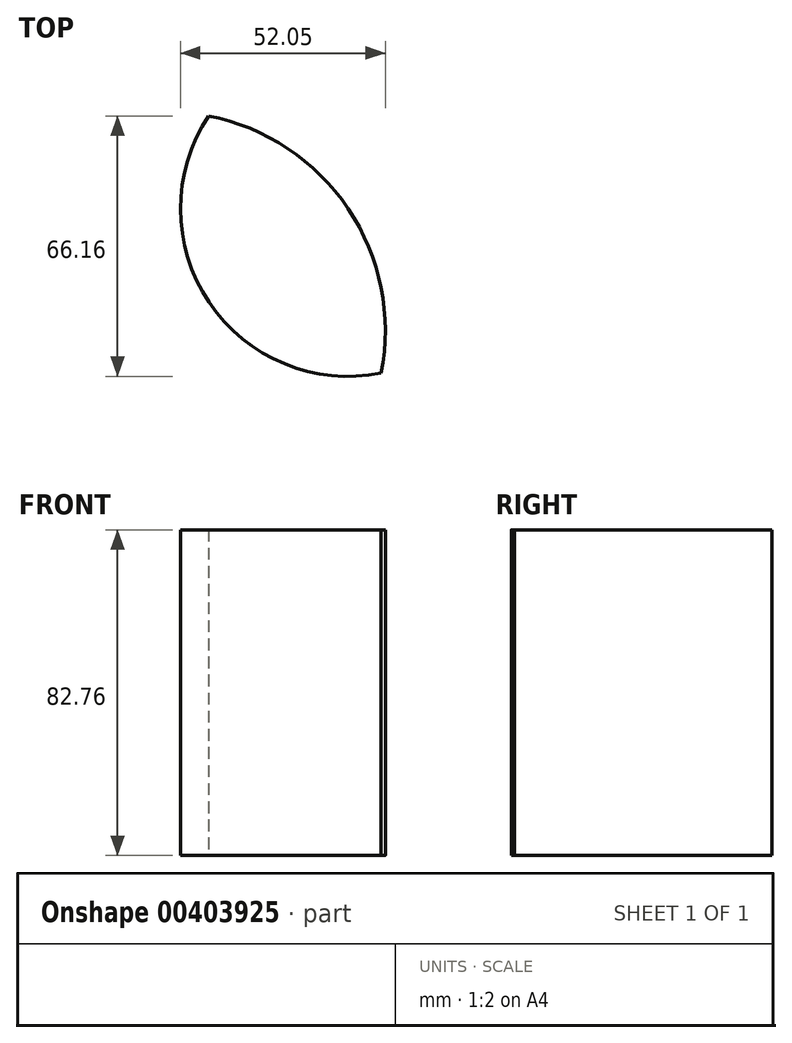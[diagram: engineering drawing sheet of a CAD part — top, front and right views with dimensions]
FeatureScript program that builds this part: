
annotation { "Feature Type Name" : "Feature", "Feature Type Description" : "" }
export const myFeature = defineFeature(function(context is Context, id is Id, definition is map)
    precondition{}
    {
        {
            var Q0;
            Q0=qCreatedBy(makeId("Top.planeOp"),FACE);
            var sketch = newSketch(context, id + "F0", { "sketchPlane" : qUnion([Q0])});
            skCircle(sketch, "E0", {"center": v(0, 0) * mm, "radius": 55.57 * mm});
            skCircle(sketch, "E1", {"center": v(46.13, 30.98) * mm, "radius": 42.6 * mm});
            skSolve(sketch);
        }
        {
            var Q0;
            {var subQ0=sQuery(id+"F0.wireOp",EDGE,"E1");var subQ1=sQuery(id+"F0.wireOp",EDGE,"E0");var subQ2=makeQuery(id+"F0.imprint","INTERSECT",VERTEX,{"disambiguationData":[OD(0.0)],"derivedFrom":[subQ1,subQ0]});Q0=makeQuery(id+"F0.imprint","IMPRINT",FACE,{"disambiguationData":[TD([[makeQuery(id+"F0.imprint","IMPRINT",EDGE,{"disambiguationData":[TD([[subQ2,1.0]])],"derivedFrom":subQ1}),1.0]])]});}
            extrude(context, id + "F1", {"entities" : qUnion([Q0]), "depth" : 82.76 * mm});
        }
    });
